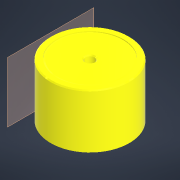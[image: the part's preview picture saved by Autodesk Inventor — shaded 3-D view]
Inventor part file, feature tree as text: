
AUTODESK INVENTOR PART (.ipt)
format: ipt  version: 2022 (Build 260153000, 153)  size: 194,048 bytes
history: native  units: mm
features: chamfer x2, sketch x2, revolve x1, plane x1, extrude x1
ambient origin geometry x8: Origin, YZ Plane, XZ Plane, XY Plane, X Axis, Y Axis, Z Axis, Center Point
bodies: Solid1 (feature_tree)
feature tree (7):
  revolve  "Revolution1"  [1 undecoded]
  chamfer  "Chamfer1"  Angle=135.0deg  [1 undecoded]
  plane  "Work Plane1"
  extrude  "Extrusion1"  TaperAngle=360.0deg  [1 undecoded]
  chamfer  "Chamfer2"  Distance=4.5mm
  sketch  "Sketch1"  dims[d0=8.0mm d1=7.0mm]
  sketch  "Sketch2"  dims[d7=135.0deg d9=135.0deg d10=360.0deg d11=4.5mm d12=9.0mm d13=16.0mm d14=22.0mm d15=0.5mm d19=44.0mm d20=66.0mm d23=1.0mm d24=2.0mm d25=45.0deg d27=6.5mm d28=49.0mm d29=5.0mm d31=67.0mm d32=4.5mm d34=1.0mm d35=0.25mm d36=1.5mm d37=78.0mm d38=5.5mm d39=0.15mm d40=0.5mm d41=4.5mm d42=6.0mm d43=5.0mm d44=10.0mm d45=0.0mm d46=1.0mm d47=2.0mm d48=45.0deg]
note: 3 required parameter values undecoded (feature->parameter linkage not recoverable at this tier; creation-order binding heuristic only, values carry confidence <= 0.55)